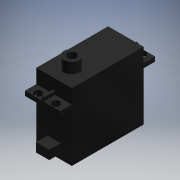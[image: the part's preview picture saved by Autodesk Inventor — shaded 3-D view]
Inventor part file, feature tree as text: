
AUTODESK INVENTOR PART (.ipt)
format: ipt  version: 2017 (Build 210142000, 142)  size: 165,376 bytes
history: native  units: mm (DEFAULTED — no unit token found)
features: extrude x7, sketch x7
ambient origin geometry x8: Origin, YZ Plane, XZ Plane, XY Plane, X Axis, Y Axis, Z Axis, Center Point
bodies: Solid1 (feature_tree)
feature tree (14):
  extrude  "Extrusion1"  Depth=47.0mm TaperAngle=0.0deg
  extrude  "Extrusion2"  Depth=6.5mm TaperAngle=0.0deg
  extrude  "Extrusion3"  Depth=1.2mm
  extrude  "Extrusion4"  TaperAngle=0.0deg  [1 undecoded]
  extrude  "Extrusion5"  Depth=12.0mm TaperAngle=0.0deg
  extrude  "Extrusion6"  [1 undecoded]
  extrude  "Extrusion8"  [1 undecoded]
  sketch  "Sketch1"  dims[d3=0.0mm d7=47.0mm d8=0.0mm d9=0.0mm]
  sketch  "Sketch2"  dims[d13=2.5mm d19=6.5mm d20=0.0mm]
  sketch  "Sketch3"  dims[d24=6.5mm d25=0.0mm d27=1.2mm]
  sketch  "Sketch4"  dims[d28=6.5mm d29=0.0mm d33=0.0mm]
  sketch  "Sketch5"  dims[d39=5.0mm d40=12.0mm d41=0.0mm]
  sketch  "Sketch6"  dims[d42=2.75mm]
  sketch  "Sketch8"
note: 3 required parameter values undecoded (feature->parameter linkage not recoverable at this tier; creation-order binding heuristic only, values carry confidence <= 0.55)
